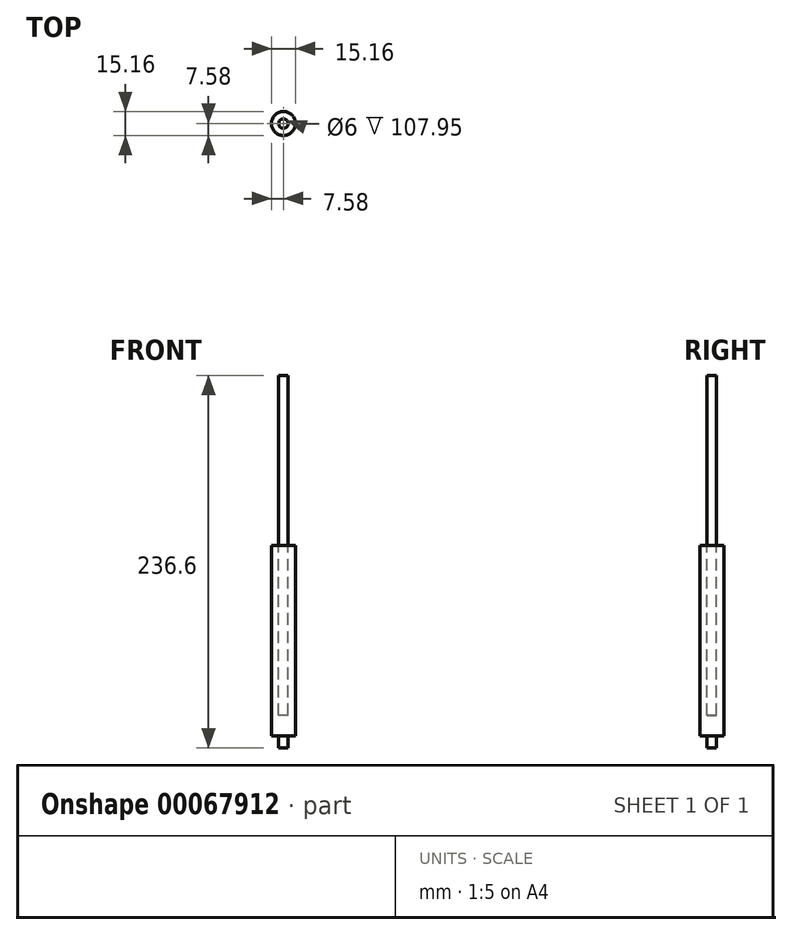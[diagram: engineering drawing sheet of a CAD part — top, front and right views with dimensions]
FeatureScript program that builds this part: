
annotation { "Feature Type Name" : "Feature", "Feature Type Description" : "" }
export const myFeature = defineFeature(function(context is Context, id is Id, definition is map)
    precondition{}
    {
        {
            var Q0;
            Q0=qCreatedBy(makeId("Top.planeOp"),FACE);
            var sketch = newSketch(context, id + "F0", { "sketchPlane" : qUnion([Q0])});
            skCircle(sketch, "E0", {"center": v(0, 0) * mm, "radius": 7.58 * mm});
            skSolve(sketch);
        }
        {
            var Q0;
            Q0=makeQuery(id+"F0.imprint","IMPRINT",FACE,{"disambiguationData":[TD([[makeQuery(id+"F0.imprint","IMPRINT",EDGE,{"derivedFrom":sQuery(id+"F0.wireOp",EDGE,"E0")}),1.0]])]});
            extrude(context, id + "F1", {"entities" : qUnion([Q0]), "depth" : 121.03 * mm});
        }
        {
            var Q0;
            Q0=makeQuery(id+"F1.opExtrude","CAP_FACE",FACE,{"disambiguationData":[OSD([sQuery(id+"F0.wireOp",EDGE,"E0")])],"isStart":true});
            var sketch = newSketch(context, id + "F2", { "sketchPlane" : qUnion([Q0])});
            skCircle(sketch, "E1", {"center": v(0, 0) * mm, "radius": 3 * mm});
            skSolve(sketch);
        }
        {
            var Q0;
            Q0=makeQuery(id+"F2.imprint","IMPRINT",FACE,{"disambiguationData":[TD([[makeQuery(id+"F2.imprint","IMPRINT",EDGE,{"derivedFrom":sQuery(id+"F2.wireOp",EDGE,"E1")}),1.0]])]});
            extrude(context, id + "F3", {"entities" : qUnion([Q0]), "operationType" : NewBodyOperationType.ADD, "depth" : 7.62 * mm});
        }
        {
            var Q0;
            Q0=makeQuery(id+"F1.opExtrude","CAP_FACE",FACE,{"disambiguationData":[OSD([sQuery(id+"F0.wireOp",EDGE,"E0")])],"isStart":false});
            var sketch = newSketch(context, id + "F4", { "sketchPlane" : qUnion([Q0])});
            skCircle(sketch, "E2", {"center": v(0, 0) * mm, "radius": 3 * mm});
            skSolve(sketch);
        }
        {
            var Q0;
            Q0=makeQuery(id+"F4.imprint","IMPRINT",FACE,{"disambiguationData":[TD([[makeQuery(id+"F4.imprint","IMPRINT",EDGE,{"derivedFrom":sQuery(id+"F4.wireOp",EDGE,"E2")}),1.0]])]});
            extrude(context, id + "F5", {"entities" : qUnion([Q0]), "operationType" : NewBodyOperationType.REMOVE, "oppositeDirection" : true, "depth" : 107.95 * mm});
        }
        {
            var Q0;
            Q0 = qSketchRegion(id + "F4", true);
            extrude(context, id + "F6", {"entities" : qUnion([Q0]), "depth" : 107.95 * mm});
        }
    });
